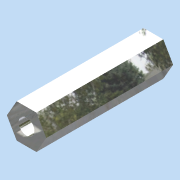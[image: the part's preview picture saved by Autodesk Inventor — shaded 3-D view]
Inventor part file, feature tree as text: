
AUTODESK INVENTOR PART (.ipt)
format: ipt  version: 2012 (Build 160160000, 160)  size: 87,552 bytes
history: native  units: in
note: dims shown in document units (in); Inventor stores cm internally (conversion verified against a paired STEP export)
features: extrude x1, sketch x1
ambient origin geometry x8: Origin, YZ Plane, XZ Plane, XY Plane, X Axis, Y Axis, Z Axis, Center Point
bodies: Solid1 (feature_tree)
feature tree (2):
  extrude  "Extrusion1"  Depth=0.215in
  sketch  "Sketch1"  dims[d0=0.1in d1=0.215in d2=0.8in d3=0.0in]
